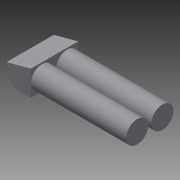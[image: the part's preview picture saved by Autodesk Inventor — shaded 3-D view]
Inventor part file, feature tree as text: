
AUTODESK INVENTOR PART (.ipt)
format: ipt  version: 2015 SP1 (Build 190203100, 203)  size: 103,424 bytes
history: native  units: in
note: dims shown in document units (in); Inventor stores cm internally (conversion verified against a paired STEP export)
features: extrude x2, sketch x1
ambient origin geometry x8: Origin, YZ Plane, XZ Plane, XY Plane, X Axis, Y Axis, Z Axis, Center Point
bodies: Solid1 (feature_tree)
feature tree (3):
  extrude  "Extrusion1"  TaperAngle=75.0deg  [1 undecoded]
  extrude  "Extrusion2"  Depth=8.0in
  sketch  "Sketch1"  dims[d1=8.0in d2=75.0deg d3=8.0in d4=3.5in d5=15.0in d6=0.0in d7=7.0in d8=7.0in d9=30.2in d10=0.0in d16=4.0in d17=4.0in]
note: 1 required parameter value undecoded (feature->parameter linkage not recoverable at this tier; creation-order binding heuristic only, values carry confidence <= 0.55)
